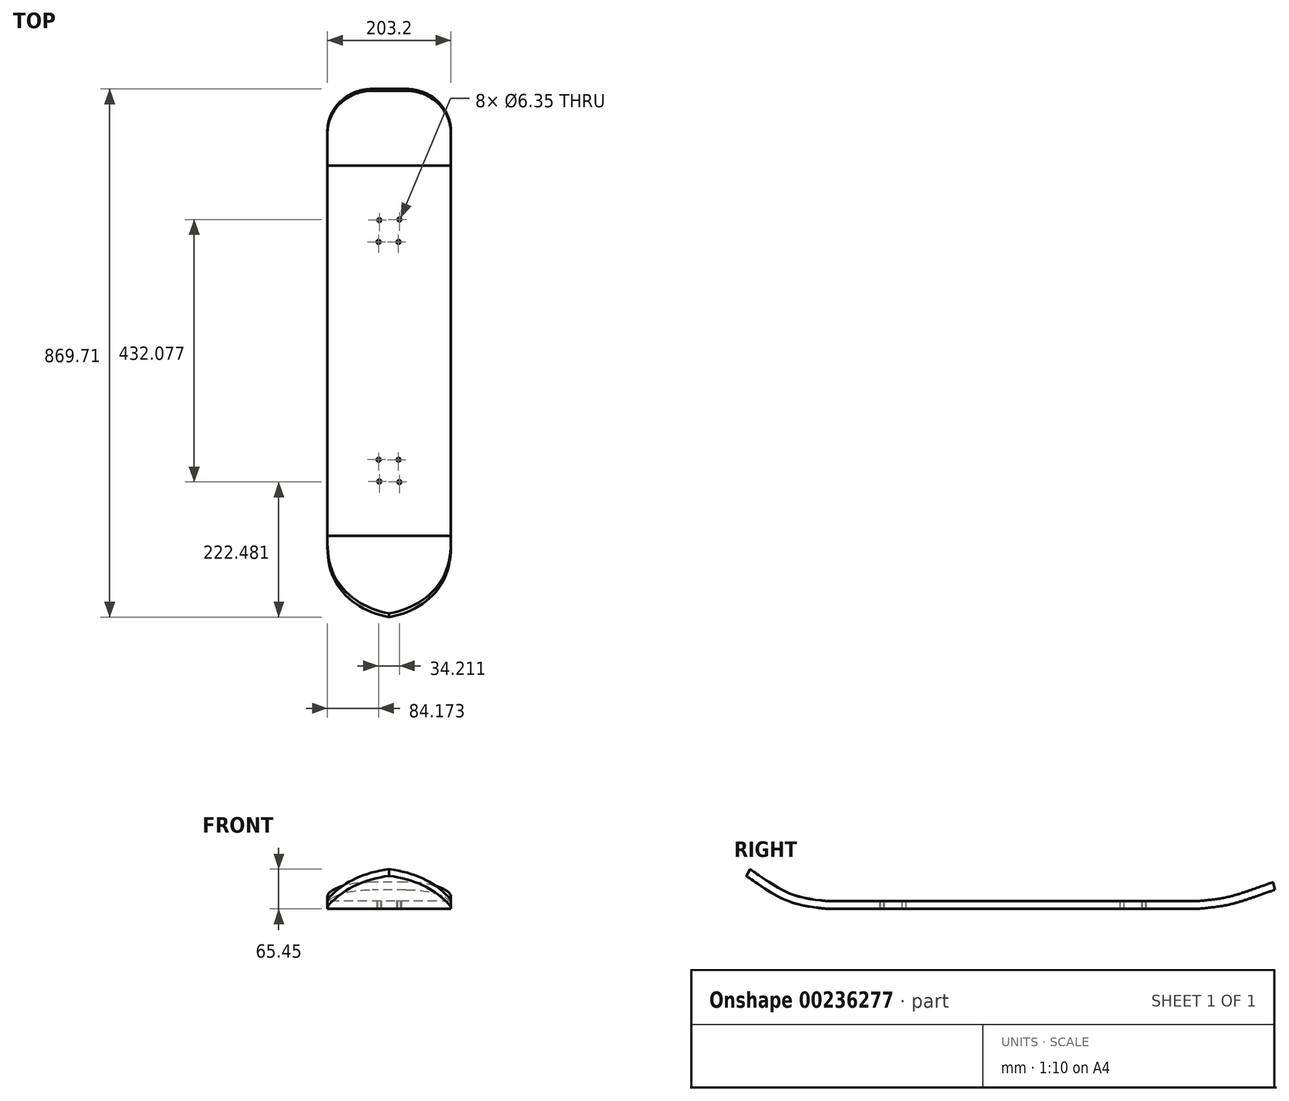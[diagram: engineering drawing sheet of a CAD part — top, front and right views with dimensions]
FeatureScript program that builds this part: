
annotation { "Feature Type Name" : "Feature", "Feature Type Description" : "" }
export const myFeature = defineFeature(function(context is Context, id is Id, definition is map)
    precondition{}
    {
        {
            var Q0;
            Q0=qCreatedBy(makeId("Top.planeOp"),FACE);
            var sketch = newSketch(context, id + "F0", { "sketchPlane" : qUnion([Q0])});
            skLineSegment(sketch, "E0.bottom", {"start": v(101.6, 304.8) * mm, "end": v(-101.6, 304.8) * mm});
            skLineSegment(sketch, "E0.top", {"start": v(101.6, -304.8) * mm, "end": v(-101.6, -304.8) * mm});
            skLineSegment(sketch, "E0.left", {"start": v(101.6, 304.8) * mm, "end": v(101.6, -304.8) * mm});
            skLineSegment(sketch, "E0.right", {"start": v(-101.6, 304.8) * mm, "end": v(-101.6, -304.8) * mm});
            skPoint(sketch, "E0.middle", {"position": v(0, 0) * mm});
            skPoint(sketch, "E1.middle", {"position": v(0, 171.06) * mm});
            skCircle(sketch, "E2", {"center": v(-16.2, 215.16) * mm, "radius": 3.18 * mm});
            skCircle(sketch, "E3", {"center": v(16.78, 216.04) * mm, "radius": 3.18 * mm});
            skCircle(sketch, "E4", {"center": v(-17.43, 179.28) * mm, "radius": 3.18 * mm});
            skCircle(sketch, "E5", {"center": v(15.34, 179.34) * mm, "radius": 3.18 * mm});
            skPoint(sketch, "E1.left.end.orphan", {"position": v(22.4, 195.82) * mm});
            skPoint(sketch, "E1.bottom.start.orphan", {"position": v(25.4, 145.66) * mm});
            skPoint(sketch, "E1.right.end.orphan", {"position": v(-25.4, 196.46) * mm});
            skPoint(sketch, "E1.right.start.orphan", {"position": v(-22.4, 146.3) * mm});
            skCircle(sketch, "E6.MirrorC", {"center": v(16.78, -216.04) * mm, "radius": 3.18 * mm});
            skCircle(sketch, "E7.MirrorC", {"center": v(15.34, -179.34) * mm, "radius": 3.18 * mm});
            skCircle(sketch, "E8.MirrorC", {"center": v(-17.43, -179.28) * mm, "radius": 3.18 * mm});
            skCircle(sketch, "E9.MirrorC", {"center": v(-16.2, -215.16) * mm, "radius": 3.18 * mm});
            skSolve(sketch);
        }
        {
            var Q0;
            Q0 = qSketchRegion(id + "F0", true);
            extrude(context, id + "F1", {"entities" : qUnion([Q0]), "endBound" : BoundingType.SYMMETRIC, "depth" : 12.7 * mm});
        }
        {
            var Q0;
            Q0=qCreatedBy(makeId("Right.planeOp"),FACE);
            var sketch = newSketch(context, id + "F2", { "sketchPlane" : qUnion([Q0])});
            skFitSpline(sketch, "E10", {"points": [v(305.2, 0) * mm, v(353.3, 6.53) * mm, v(394.85, 19) * mm], "startDerivative": vector(95.64, 9.38) * mm, "endDerivative": vector(83.57, 28.8) * mm});
            skFitSpline(sketch, "E11", {"points": [v(394.85, 19) * mm, v(430.06, 31.35) * mm], "startDerivative": vector(35.2, 12.35) * mm, "endDerivative": vector(35.2, 12.35) * mm});
            skFitSpline(sketch, "E12", {"points": [v(-303.58, 0) * mm, v(-361.47, 10.2) * mm, v(-405.58, 33.17) * mm, v(-437.74, 55.22) * mm], "startDerivative": vector(-164.14, 17.05) * mm, "endDerivative": vector(-103.8, 73.05) * mm});
            skSolve(sketch);
        }
        {
            var Q0;
            Q0=makeQuery(id+"F1.opExtrude","SWEPT_FACE",FACE,{"disambiguationData":[OSD([sQuery(id+"F0.wireOp",EDGE,"E0.bottom")])]});
            var Q1;
            Q1=sQuery(id+"F2.wireOp",EDGE,"E10");
            var Q2;
            Q2=sQuery(id+"F2.wireOp",EDGE,"E11");
            sweep(context, id + "F3", {"operationType" : NewBodyOperationType.ADD, "profiles" : qUnion([Q0]), "path" : qUnion([Q1, Q2])});
        }
        {
            var Q0;
            Q0=makeQuery(id+"F1.opExtrude","SWEPT_FACE",FACE,{"disambiguationData":[OSD([sQuery(id+"F0.wireOp",EDGE,"E0.top")])]});
            var Q1;
            Q1=sQuery(id+"F2.wireOp",EDGE,"E12");
            sweep(context, id + "F4", {"operationType" : NewBodyOperationType.ADD, "profiles" : qUnion([Q0]), "path" : qUnion([Q1])});
        }
        {
            var Q0;
            Q0=makeQuery(id+"F4.opSweep","CAP_EDGE",EDGE,{"disambiguationData":[OSD([sQuery(id+"F0.wireOp",EDGE,"E0.top"),sQuery(id+"F0.wireOp",EDGE,"E0.left"),sQuery(id+"F2.wireOp",VERTEX,"E12.end")])],"isStart":false});
            var Q1;
            Q1=makeQuery(id+"F4.opSweep","CAP_EDGE",EDGE,{"disambiguationData":[OSD([sQuery(id+"F0.wireOp",EDGE,"E0.top"),sQuery(id+"F0.wireOp",EDGE,"E0.right"),sQuery(id+"F2.wireOp",VERTEX,"E12.end")])],"isStart":false});
            fillet(context, id + "F5", {"entities" : qUnion([Q0, Q1]), "radius" : 128.77 * mm, "tangentPropagation" : true, "allowEdgeOverflow" : false});
        }
        {
            var Q0;
            Q0=makeQuery(id+"F3.opSweep","CAP_EDGE",EDGE,{"disambiguationData":[OSD([sQuery(id+"F0.wireOp",EDGE,"E0.bottom"),sQuery(id+"F0.wireOp",EDGE,"E0.right"),sQuery(id+"F2.wireOp",VERTEX,"E11.end")])],"isStart":false});
            var Q1;
            Q1=makeQuery(id+"F3.opSweep","CAP_EDGE",EDGE,{"disambiguationData":[OSD([sQuery(id+"F0.wireOp",EDGE,"E0.bottom"),sQuery(id+"F0.wireOp",EDGE,"E0.left"),sQuery(id+"F2.wireOp",VERTEX,"E11.end")])],"isStart":false});
            fillet(context, id + "F6", {"entities" : qUnion([Q0, Q1]), "radius" : 73.6 * mm, "tangentPropagation" : true, "allowEdgeOverflow" : false});
        }
    });
